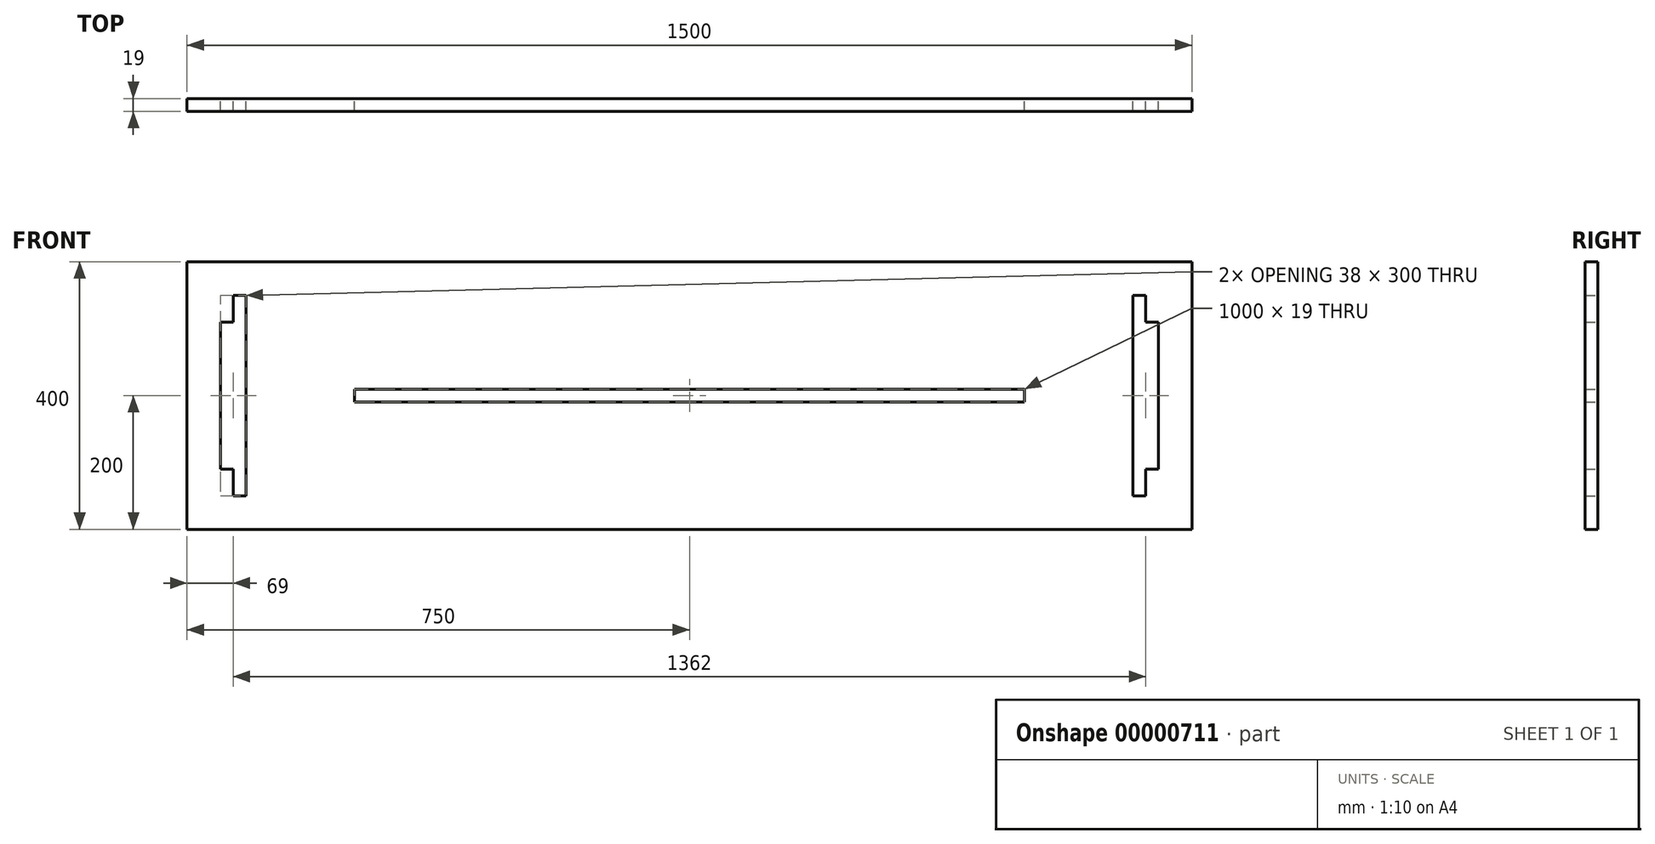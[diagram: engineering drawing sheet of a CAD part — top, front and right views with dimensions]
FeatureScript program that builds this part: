
annotation { "Feature Type Name" : "Feature", "Feature Type Description" : "" }
export const myFeature = defineFeature(function(context is Context, id is Id, definition is map)
    precondition{}
    {
        {
            var Q0;
            Q0=qCreatedBy(makeId("Front.planeOp"),FACE);
            var sketch = newSketch(context, id + "F0", { "sketchPlane" : qUnion([Q0])});
            skLineSegment(sketch, "E0.rect.bottom", {"start": v(-750, 200) * mm, "end": v(750, 200) * mm});
            skLineSegment(sketch, "E0.rect.top", {"start": v(-750, -200) * mm, "end": v(750, -200) * mm});
            skLineSegment(sketch, "E0.rect.left", {"start": v(-750, 200) * mm, "end": v(-750, -200) * mm});
            skLineSegment(sketch, "E0.rect.right", {"start": v(750, 200) * mm, "end": v(750, -200) * mm});
            skPoint(sketch, "E0.rect.middle", {"position": v(0, 0) * mm});
            skLineSegment(sketch, "E1", {"start": v(-681, 150) * mm, "end": v(-662, 150) * mm});
            skLineSegment(sketch, "E2", {"start": v(-662, 150) * mm, "end": v(-662, -150) * mm});
            skLineSegment(sketch, "E3", {"start": v(-662, -150) * mm, "end": v(-681, -150) * mm});
            skLineSegment(sketch, "E4", {"start": v(-681, -150) * mm, "end": v(-681, -110) * mm});
            skLineSegment(sketch, "E5", {"start": v(-681, -110) * mm, "end": v(-700, -110) * mm});
            skLineSegment(sketch, "E6", {"start": v(-700, -110) * mm, "end": v(-700, 110) * mm});
            skLineSegment(sketch, "E7", {"start": v(-700, 110) * mm, "end": v(-681, 110) * mm});
            skLineSegment(sketch, "E8", {"start": v(-681, 110) * mm, "end": v(-681, 150) * mm});
            skLineSegment(sketch, "E9", {"start": v(-750, 0) * mm, "end": v(-700, 0) * mm, "construction": true});
            skLineSegment(sketch, "E10", {"start": v(662, 150) * mm, "end": v(681, 150) * mm});
            skLineSegment(sketch, "E11", {"start": v(681, 150) * mm, "end": v(681, 110) * mm});
            skLineSegment(sketch, "E12", {"start": v(681, 110) * mm, "end": v(700, 110) * mm});
            skLineSegment(sketch, "E13", {"start": v(700, 110) * mm, "end": v(700, -110) * mm});
            skLineSegment(sketch, "E14", {"start": v(700, -110) * mm, "end": v(681, -110) * mm});
            skLineSegment(sketch, "E15", {"start": v(681, -110) * mm, "end": v(681, -150) * mm});
            skLineSegment(sketch, "E16", {"start": v(681, -150) * mm, "end": v(662, -150) * mm});
            skLineSegment(sketch, "E17", {"start": v(662, -150) * mm, "end": v(662, 150) * mm});
            skLineSegment(sketch, "E18", {"start": v(700, 0) * mm, "end": v(750, 0) * mm, "construction": true});
            skLineSegment(sketch, "E19.rect.bottom", {"start": v(-500, 9.5) * mm, "end": v(500, 9.5) * mm});
            skLineSegment(sketch, "E19.rect.top", {"start": v(-500, -9.5) * mm, "end": v(500, -9.5) * mm});
            skLineSegment(sketch, "E19.rect.left", {"start": v(-500, 9.5) * mm, "end": v(-500, -9.5) * mm});
            skLineSegment(sketch, "E19.rect.right", {"start": v(500, 9.5) * mm, "end": v(500, -9.5) * mm});
            skSolve(sketch);
        }
        {
            var Q0;
            Q0=makeQuery(id+"F0.imprint","IMPRINT",FACE,{"disambiguationData":[TD([[makeQuery(id+"F0.imprint","IMPRINT",EDGE,{"derivedFrom":sQuery(id+"F0.wireOp",EDGE,"E0.rect.bottom")}),-1.0]])]});
            extrude(context, id + "F1", {"entities" : qUnion([Q0]), "depth" : 19 * mm});
        }
    });
